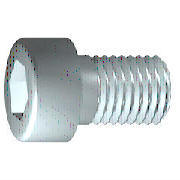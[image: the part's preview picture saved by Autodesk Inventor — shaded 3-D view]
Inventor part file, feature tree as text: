
AUTODESK INVENTOR PART (.ipt)
format: ipt  version: 2022 (Build 260153000, 153)  size: 193,536 bytes
history: native  units: mm (DEFAULTED — no unit token found)
features: sketch x2, other x1, extrude x1, plane x1, fillet x1
ambient origin geometry x7: Origin, YZ Plane, XY Plane, X Axis, Y Axis, Z Axis, Center Point
bodies: Solid1 (feature_tree)
feature tree (6):
  other  "Базовый элемент"
  extrude  "Паз"  Depth=8.65mm
  plane  "Work Plane1"
  fillet  "Fillet2"  Radius=0.276153mm
  sketch  "Эскиз1"
  sketch  "Эскиз2"
